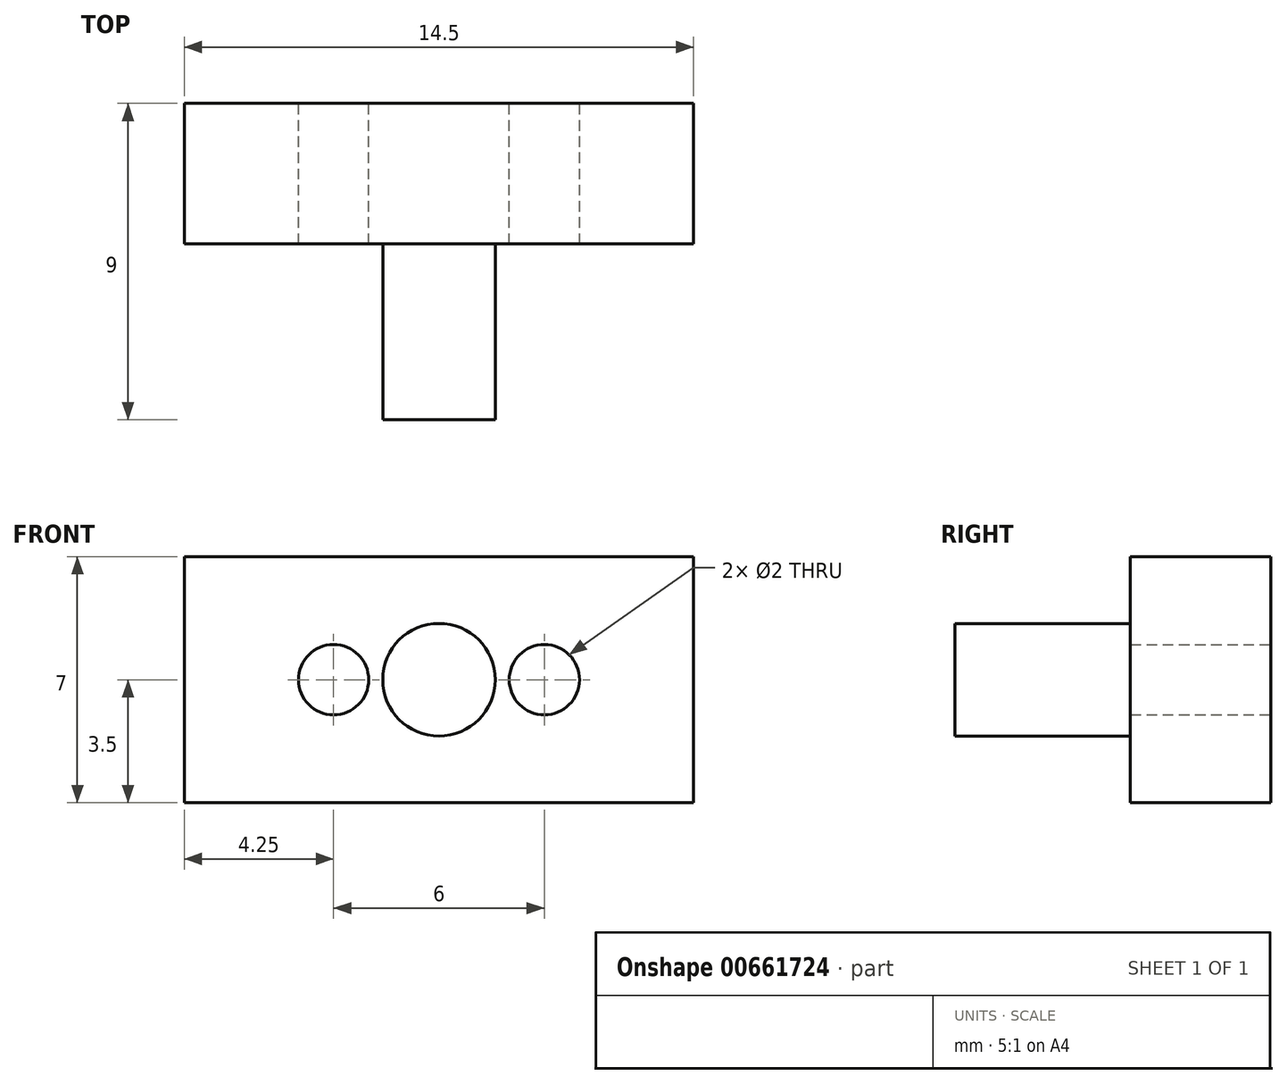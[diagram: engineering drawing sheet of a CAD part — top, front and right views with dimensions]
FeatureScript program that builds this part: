
annotation { "Feature Type Name" : "Feature", "Feature Type Description" : "" }
export const myFeature = defineFeature(function(context is Context, id is Id, definition is map)
    precondition{}
    {
        {
            var Q0;
            Q0=qCreatedBy(makeId("Front.planeOp"),FACE);
            var sketch = newSketch(context, id + "F0", { "sketchPlane" : qUnion([Q0])});
            skLineSegment(sketch, "E0.bottom", {"start": v(-7.25, 3.5) * mm, "end": v(7.25, 3.5) * mm});
            skLineSegment(sketch, "E0.top", {"start": v(-7.25, -3.5) * mm, "end": v(7.25, -3.5) * mm});
            skLineSegment(sketch, "E0.left", {"start": v(-7.25, 3.5) * mm, "end": v(-7.25, -3.5) * mm});
            skLineSegment(sketch, "E0.right", {"start": v(7.25, 3.5) * mm, "end": v(7.25, -3.5) * mm});
            skPoint(sketch, "E0.middle", {"position": v(0, 0) * mm});
            skCircle(sketch, "E1", {"center": v(-3, 0) * mm, "radius": 1 * mm});
            skCircle(sketch, "E2", {"center": v(3, 0) * mm, "radius": 1 * mm});
            skSolve(sketch);
        }
        {
            var Q0;
            Q0 = qSketchRegion(id + "F0", true);
            extrude(context, id + "F1", {"entities" : qUnion([Q0]), "depth" : 4 * mm, "offsetDistance" : 25 * mm});
        }
        {
            var Q0;
            Q0=makeQuery(id+"F1.opExtrude","CAP_FACE",FACE,{"disambiguationData":[OSD([sQuery(id+"F0.wireOp",EDGE,"E0.bottom"),sQuery(id+"F0.wireOp",EDGE,"E0.top"),sQuery(id+"F0.wireOp",EDGE,"E0.left"),sQuery(id+"F0.wireOp",EDGE,"E0.right"),sQuery(id+"F0.wireOp",EDGE,"E1"),sQuery(id+"F0.wireOp",EDGE,"E2")])],"isStart":false});
            var sketch = newSketch(context, id + "F2", { "sketchPlane" : qUnion([Q0])});
            skCircle(sketch, "E3", {"center": v(0, 0) * mm, "radius": 1.6 * mm});
            skSolve(sketch);
        }
        {
            var Q0;
            Q0=makeQuery(id+"F2.imprint","IMPRINT",FACE,{"disambiguationData":[TD([[makeQuery(id+"F2.imprint","IMPRINT",EDGE,{"derivedFrom":sQuery(id+"F2.wireOp",EDGE,"E3")}),1.0]])]});
            extrude(context, id + "F3", {"entities" : qUnion([Q0]), "operationType" : NewBodyOperationType.ADD, "depth" : 5 * mm, "offsetDistance" : 25 * mm});
        }
    });
